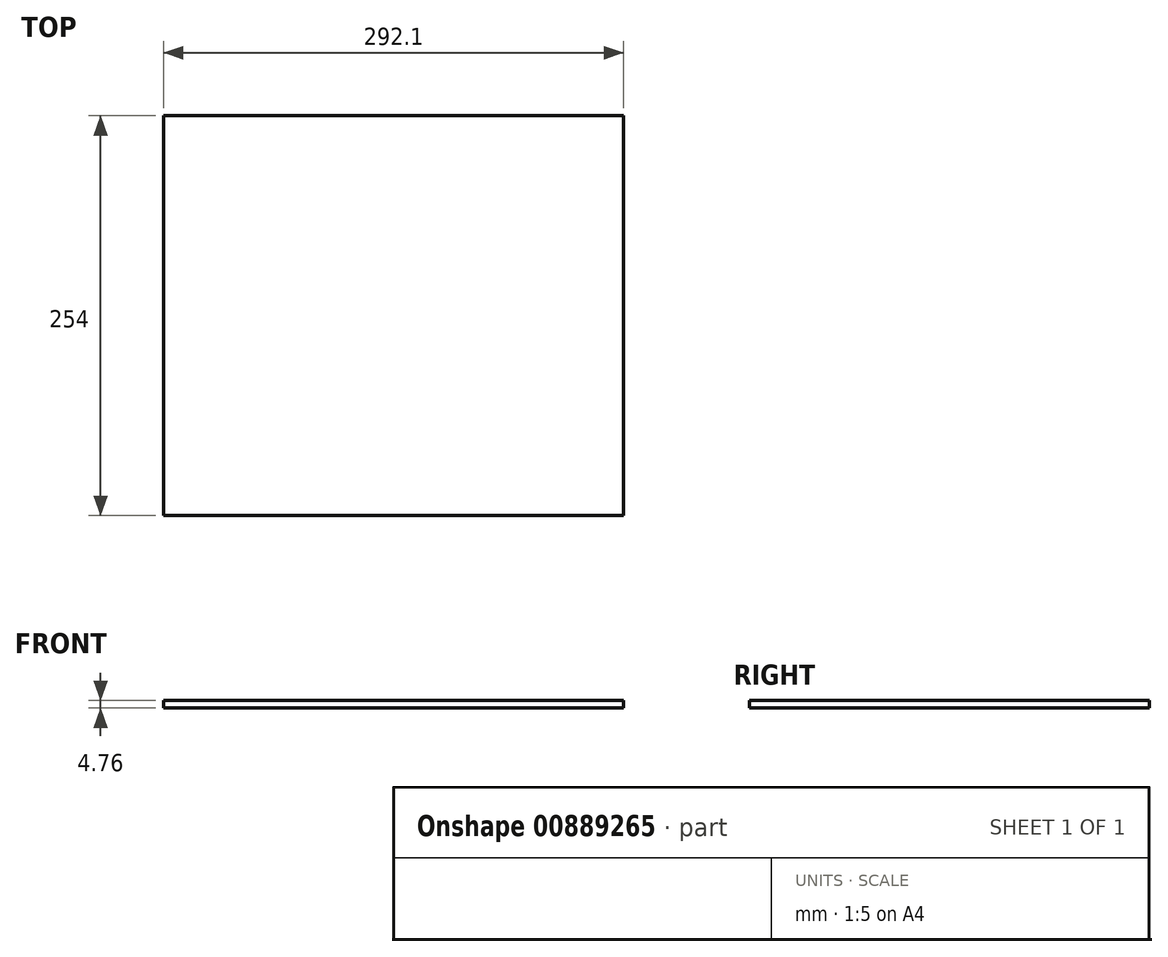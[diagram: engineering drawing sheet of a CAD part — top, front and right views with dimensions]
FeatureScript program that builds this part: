
annotation { "Feature Type Name" : "Feature", "Feature Type Description" : "" }
export const myFeature = defineFeature(function(context is Context, id is Id, definition is map)
    precondition{}
    {
        {
            var Q0;
            Q0=qCreatedBy(makeId("Front.planeOp"),FACE);
            var sketch = newSketch(context, id + "F0", { "sketchPlane" : qUnion([Q0])});
            skLineSegment(sketch, "E0.bottom", {"start": v(0, 0) * mm, "end": v(292.1, 0) * mm});
            skLineSegment(sketch, "E0.top", {"start": v(0, 4.76) * mm, "end": v(292.1, 4.76) * mm});
            skLineSegment(sketch, "E0.left", {"start": v(0, 0) * mm, "end": v(0, 4.76) * mm});
            skLineSegment(sketch, "E0.right", {"start": v(292.1, 0) * mm, "end": v(292.1, 4.76) * mm});
            skSolve(sketch);
        }
        {
            var Q0;
            Q0 = qSketchRegion(id + "F0", true);
            extrude(context, id + "F1", {"entities" : qUnion([Q0]), "oppositeDirection" : true, "depth" : 254 * mm, "offsetDistance" : 25.4 * mm});
        }
    });
